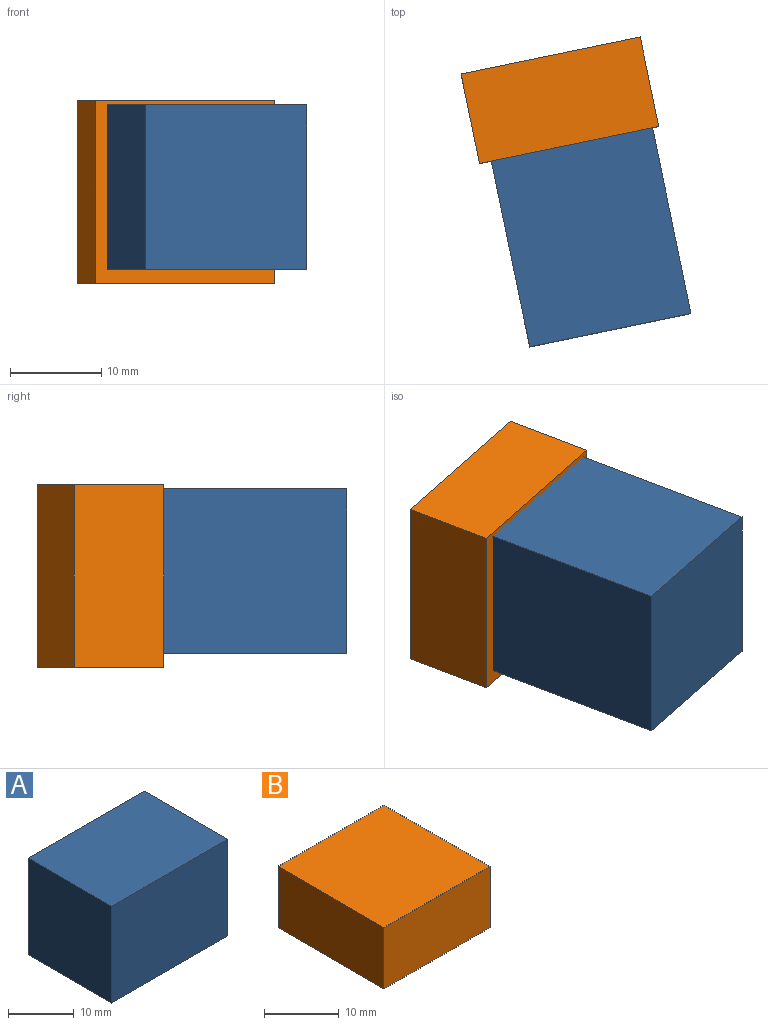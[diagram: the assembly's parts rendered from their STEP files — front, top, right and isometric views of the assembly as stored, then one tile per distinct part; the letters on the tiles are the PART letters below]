
ASSEMBLY  parts=2 mates=1
PART A: 6 faces, bbox 25x18x18 mm
  f0: plane 25x18mm, normal (0,0,1), area 450mm2, adj f1,f3,f4,f5
  f1: plane 25x18mm, normal (0,-1,0), area 450mm2, adj f0,f2,f4,f5
  f2: plane 25x18mm, normal (0,0,-1), area 450mm2, adj f1,f3,f4,f5
  f3: plane 25x18mm, normal (0,1,0), area 450mm2, adj f0,f2,f4,f5
  f4: plane 18x18mm, normal (1,0,0), area 324mm2, adj f0,f1,f2,f3
  f5: plane 18x18mm, normal (-1,0,0), area 324mm2, adj f0,f1,f2,f3
PART B: 6 faces, bbox 20x20x10 mm
  f0: plane 20x10mm, normal (0,1,0), area 200mm2, adj f1,f3,f4,f5
  f1: plane 20x10mm, normal (-1,0,0), area 200mm2, adj f0,f2,f4,f5
  f2: plane 20x10mm, normal (0,-1,0), area 200mm2, adj f1,f3,f4,f5
  f3: plane 20x10mm, normal (1,0,0), area 200mm2, adj f0,f2,f4,f5
  f4: plane 20x20mm, normal (0,0,1), area 400mm2, adj f0,f1,f2,f3
  f5: plane 20x20mm, normal (0,0,-1), area 400mm2, adj f0,f1,f2,f3
PLACE A rot(axis=(0,0,-1),78.3deg) t=(2.37,-7.62,-51.4)mm
PLACE B rot(axis=(-0.53,-0.66,-0.53),113.5deg) t=(8.21,-26.58,33.06)mm
MATE parallel B.f4 <-> A.f5  axis (-0.2,0.98,0) through (10.27,-15.95,38.55)mm
